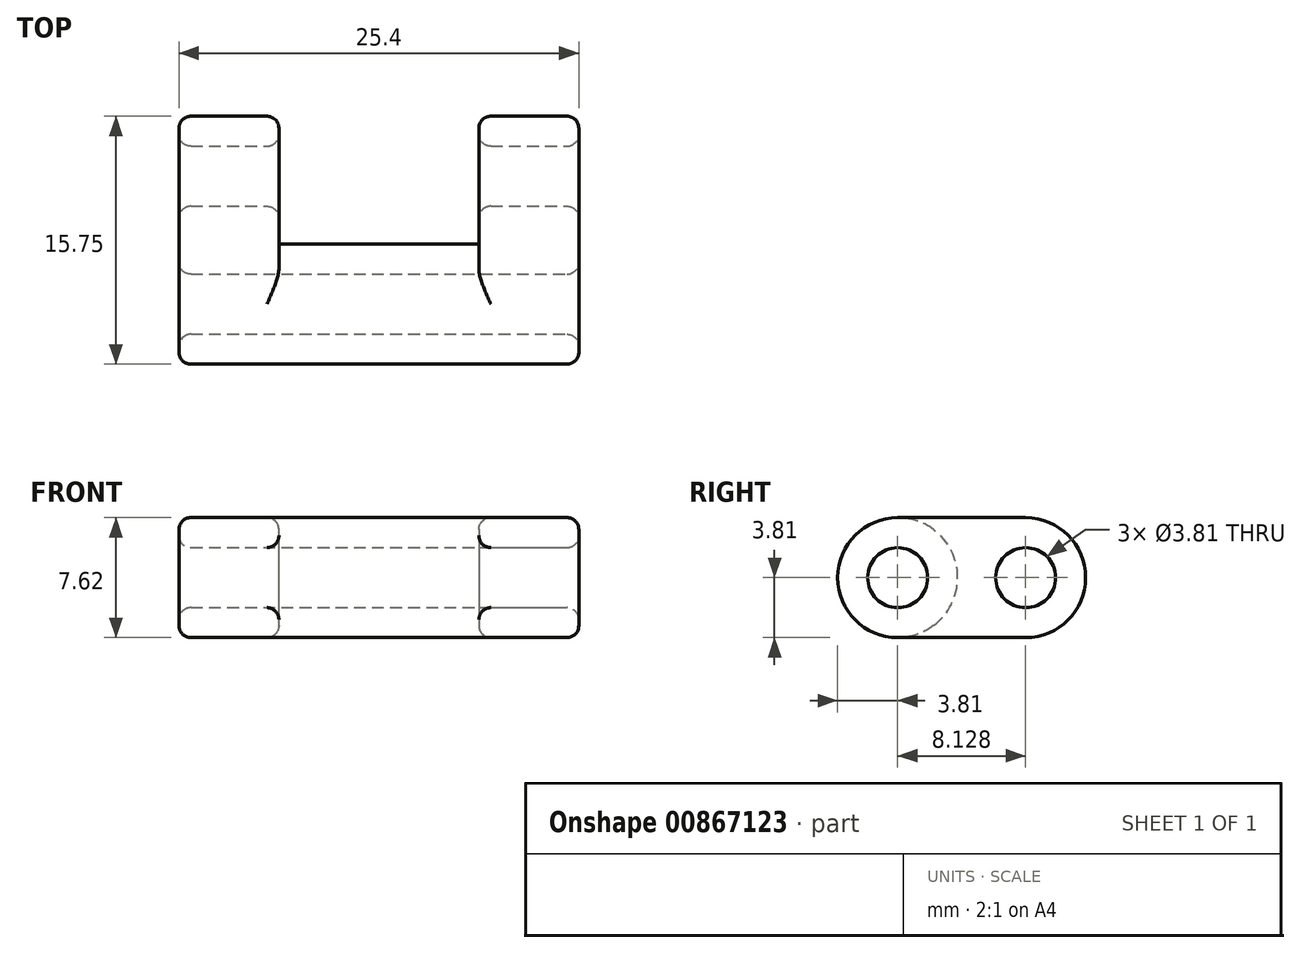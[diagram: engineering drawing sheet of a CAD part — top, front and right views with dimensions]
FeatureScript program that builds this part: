
annotation { "Feature Type Name" : "Feature", "Feature Type Description" : "" }
export const myFeature = defineFeature(function(context is Context, id is Id, definition is map)
    precondition{}
    {
        {
            var Q0;
            Q0=qCreatedBy(makeId("Top.planeOp"),FACE);
            var sketch = newSketch(context, id + "F0", { "sketchPlane" : qUnion([Q0])});
            skLineSegment(sketch, "E0", {"start": v(0, 0) * mm, "end": v(0, 15.75) * mm});
            skLineSegment(sketch, "E1", {"start": v(0, 15.75) * mm, "end": v(6.35, 15.75) * mm});
            skLineSegment(sketch, "E2", {"start": v(6.35, 15.75) * mm, "end": v(6.35, 7.62) * mm});
            skLineSegment(sketch, "E3", {"start": v(6.35, 7.62) * mm, "end": v(19.05, 7.62) * mm});
            skLineSegment(sketch, "E4", {"start": v(19.05, 7.62) * mm, "end": v(19.05, 15.75) * mm});
            skLineSegment(sketch, "E5", {"start": v(19.05, 15.75) * mm, "end": v(25.4, 15.75) * mm});
            skLineSegment(sketch, "E6", {"start": v(25.4, 15.75) * mm, "end": v(25.4, 0) * mm});
            skLineSegment(sketch, "E7", {"start": v(25.4, 0) * mm, "end": v(0, 0) * mm});
            skSolve(sketch);
        }
        {
            var Q0;
            Q0=makeQuery(id+"F0.imprint","IMPRINT",FACE,{"disambiguationData":[TD([[makeQuery(id+"F0.imprint","IMPRINT",EDGE,{"derivedFrom":sQuery(id+"F0.wireOp",EDGE,"E0")}),-1.0]])]});
            extrude(context, id + "F1", {"entities" : qUnion([Q0]), "depth" : 7.62 * mm, "offsetDistance" : 25.4 * mm});
        }
        {
            var Q0;
            Q0=makeQuery(id+"F1.opExtrude","CAP_EDGE",EDGE,{"disambiguationData":[OSD([sQuery(id+"F0.wireOp",EDGE,"E7")])],"isStart":false});
            var Q1;
            Q1=makeQuery(id+"F1.opExtrude","CAP_EDGE",EDGE,{"disambiguationData":[OSD([sQuery(id+"F0.wireOp",EDGE,"E7")])],"isStart":true});
            var Q2;
            Q2=makeQuery(id+"F1.opExtrude","CAP_EDGE",EDGE,{"disambiguationData":[OSD([sQuery(id+"F0.wireOp",EDGE,"E5")])],"isStart":false});
            var Q3;
            Q3=makeQuery(id+"F1.opExtrude","CAP_EDGE",EDGE,{"disambiguationData":[OSD([sQuery(id+"F0.wireOp",EDGE,"E5")])],"isStart":true});
            var Q4;
            Q4=makeQuery(id+"F1.opExtrude","CAP_EDGE",EDGE,{"disambiguationData":[OSD([sQuery(id+"F0.wireOp",EDGE,"E3")])],"isStart":false});
            var Q5;
            Q5=makeQuery(id+"F1.opExtrude","CAP_EDGE",EDGE,{"disambiguationData":[OSD([sQuery(id+"F0.wireOp",EDGE,"E3")])],"isStart":true});
            var Q6;
            Q6=makeQuery(id+"F1.opExtrude","CAP_EDGE",EDGE,{"disambiguationData":[OSD([sQuery(id+"F0.wireOp",EDGE,"E1")])],"isStart":false});
            var Q7;
            Q7=makeQuery(id+"F1.opExtrude","CAP_EDGE",EDGE,{"disambiguationData":[OSD([sQuery(id+"F0.wireOp",EDGE,"E1")])],"isStart":true});
            fillet(context, id + "F2", {"entities" : qUnion([Q0, Q1, Q2, Q3, Q4, Q5, Q6, Q7]), "radius" : 3.8 * mm, "tangentPropagation" : true, "allowEdgeOverflow" : false});
        }
        {
            var Q0;
            Q0=makeQuery(id+"F1.opExtrude","SWEPT_FACE",FACE,{"disambiguationData":[OSD([sQuery(id+"F0.wireOp",EDGE,"E6")])]});
            var sketch = newSketch(context, id + "F3", { "sketchPlane" : qUnion([Q0])});
            skCircle(sketch, "E8", {"center": v(3.81, 3.81) * mm, "radius": 1.9 * mm});
            skCircle(sketch, "E9", {"center": v(11.94, 3.81) * mm, "radius": 1.9 * mm});
            skSolve(sketch);
        }
        {
            var Q0;
            Q0=makeQuery(id+"F3.imprint","IMPRINT",FACE,{"disambiguationData":[TD([[makeQuery(id+"F3.imprint","IMPRINT",EDGE,{"derivedFrom":sQuery(id+"F3.wireOp",EDGE,"E8")}),1.0]])]});
            var Q1;
            Q1=makeQuery(id+"F3.imprint","IMPRINT",FACE,{"disambiguationData":[TD([[makeQuery(id+"F3.imprint","IMPRINT",EDGE,{"derivedFrom":sQuery(id+"F3.wireOp",EDGE,"E9")}),1.0]])]});
            extrude(context, id + "F4", {"entities" : qUnion([Q0, Q1]), "operationType" : NewBodyOperationType.REMOVE, "oppositeDirection" : true, "depth" : 25.4 * mm, "offsetDistance" : 25.4 * mm});
        }
        {
            var Q0;
            Q0=makeQuery(id+"F1.opExtrude","SWEPT_FACE",FACE,{"disambiguationData":[OSD([sQuery(id+"F0.wireOp",EDGE,"E6")])]});
            var Q1;
            Q1=makeQuery(id+"F1.opExtrude","SWEPT_FACE",FACE,{"disambiguationData":[OSD([sQuery(id+"F0.wireOp",EDGE,"E0")])]});
            var Q2;
            Q2=makeQuery(id+"F2.opFillet","BLEND_EDGE",EDGE,{"blendedFrom":[makeQuery(id+"F1.opExtrude","CAP_EDGE",EDGE,{"disambiguationData":[OSD([sQuery(id+"F0.wireOp",EDGE,"E1")])],"isStart":true}),makeQuery(id+"F1.opExtrude","SWEPT_FACE",FACE,{"disambiguationData":[OSD([sQuery(id+"F0.wireOp",EDGE,"E2")])]})],"blendedInto":[makeQuery(id+"F1.opExtrude","SWEPT_FACE",FACE,{"disambiguationData":[OSD([sQuery(id+"F0.wireOp",EDGE,"E2")])]})]});
            var Q3;
            Q3=makeQuery(id+"F4.boolean.opBoolean","INTERSECT",EDGE,{"derivedFrom":[makeQuery(id+"F1.opExtrude","SWEPT_FACE",FACE,{"disambiguationData":[OSD([sQuery(id+"F0.wireOp",EDGE,"E2")])]}),makeQuery(id+"F4.opExtrude","SWEPT_FACE",FACE,{"disambiguationData":[OSD([sQuery(id+"F3.wireOp",EDGE,"E9")])]})]});
            var Q4;
            Q4=makeQuery(id+"F4.boolean.opBoolean","INTERSECT",EDGE,{"derivedFrom":[makeQuery(id+"F1.opExtrude","SWEPT_FACE",FACE,{"disambiguationData":[OSD([sQuery(id+"F0.wireOp",EDGE,"E4")])]}),makeQuery(id+"F4.opExtrude","SWEPT_FACE",FACE,{"disambiguationData":[OSD([sQuery(id+"F3.wireOp",EDGE,"E9")])]})]});
            var Q5;
            Q5=makeQuery(id+"F2.opFillet","BLEND_EDGE",EDGE,{"blendedFrom":[makeQuery(id+"F1.opExtrude","CAP_EDGE",EDGE,{"disambiguationData":[OSD([sQuery(id+"F0.wireOp",EDGE,"E5")])],"isStart":true}),makeQuery(id+"F1.opExtrude","SWEPT_FACE",FACE,{"disambiguationData":[OSD([sQuery(id+"F0.wireOp",EDGE,"E4")])]})],"blendedInto":[makeQuery(id+"F1.opExtrude","SWEPT_FACE",FACE,{"disambiguationData":[OSD([sQuery(id+"F0.wireOp",EDGE,"E4")])]})]});
            fillet(context, id + "F5", {"entities" : qUnion([Q0, Q1, Q2, Q3, Q4, Q5]), "radius" : 0.76 * mm, "tangentPropagation" : true, "allowEdgeOverflow" : false});
        }
    });
